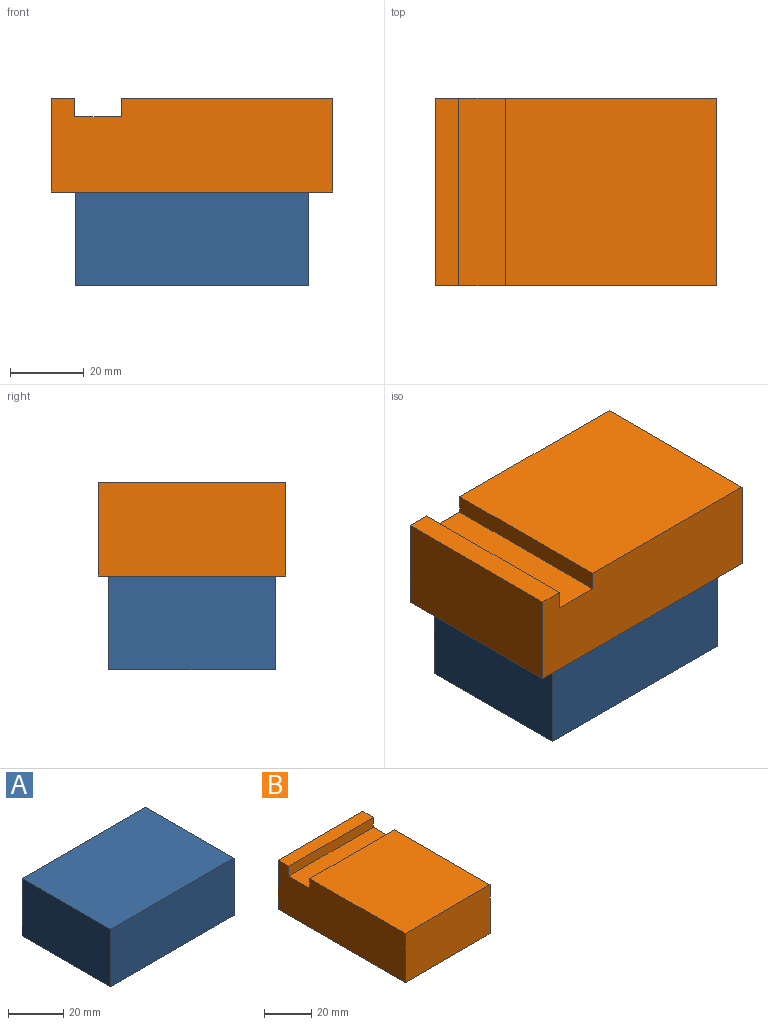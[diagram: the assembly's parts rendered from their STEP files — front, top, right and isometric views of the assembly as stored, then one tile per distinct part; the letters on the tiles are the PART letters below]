
ASSEMBLY  parts=2 mates=1
PART A: 6 faces, bbox 63.3x45.2x25.4 mm
  f0: plane 45.15x25.4mm, normal (1,0,0), area 1146.9mm2, adj f1,f3,f4,f5
  f1: plane 63.28x25.4mm, normal (0,1,0), area 1607.2mm2, adj f0,f2,f4,f5
  f2: plane 45.15x25.4mm, normal (-1,0,0), area 1146.9mm2, adj f1,f3,f4,f5
  f3: plane 63.28x25.4mm, normal (0,-1,0), area 1607.2mm2, adj f0,f2,f4,f5
  f4: plane 63.28x45.15mm, normal (0,0,1), area 2857.2mm2, adj f0,f1,f2,f3
  f5: plane 63.28x45.15mm, normal (0,0,-1), area 2857.2mm2, adj f0,f1,f2,f3
PART B: 10 faces, bbox 50.8x76.2x25.4 mm
  f0: plane 50.8x6.35mm, normal (0,0,1), area 322.6mm2, adj f1,f2,f3,f7
  f1: plane 76.2x25.4mm, normal (-1,0,0), area 1871mm2, adj f0,f3,f4,f5,f6,f7,f8,f9
  f2: plane 76.2x25.4mm, normal (1,0,0), area 1871mm2, adj f0,f3,f4,f5,f6,f7,f8,f9
  f3: plane 50.8x25.4mm, normal (0,1,0), area 1290.3mm2, adj f0,f1,f2,f6
  f4: plane 50.8x25.4mm, normal (0,-1,0), area 1290.3mm2, adj f1,f2,f5,f6
  f5: plane 57.15x50.8mm, normal (0,0,1), area 2903.2mm2, adj f1,f2,f4,f8
  f6: plane 76.2x50.8mm, normal (0,0,-1), area 3871mm2, adj f1,f2,f3,f4
  f7: plane 50.8x5.08mm, normal (0,-1,0), area 258.1mm2, adj f0,f1,f2,f9
  f8: plane 50.8x5.08mm, normal (0,1,0), area 258.1mm2, adj f1,f2,f5,f9
  f9: plane 50.8x12.7mm, normal (0,0,1), area 645.2mm2, adj f1,f2,f7,f8
PLACE A t=(6.66,16.39,-32.1)mm
PLACE B rot(axis=(0,0,1),90deg) t=(6.66,16.39,6)mm fixed
MATE fastened A.f4 <-> B.f6  axis (0,0,1) through (6.66,16.39,-6.7)mm
